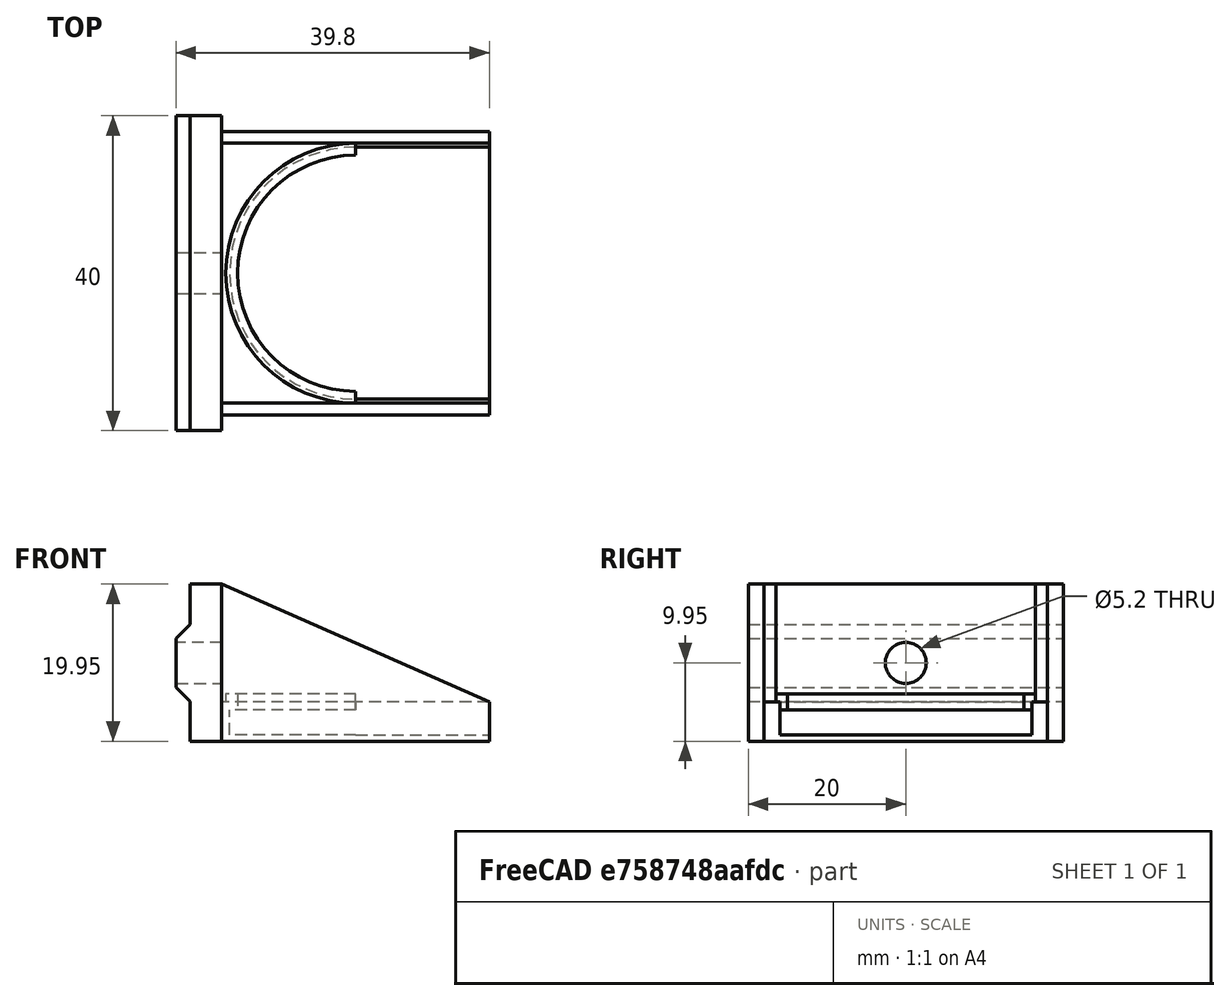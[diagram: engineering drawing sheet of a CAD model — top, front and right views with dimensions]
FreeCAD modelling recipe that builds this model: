
FCSTD DOCUMENT  (FreeCAD 1.0R39109 (Git))
Label: plotter_magnet_mount
License: All rights reserved
LicenseURL: https://en.wikipedia.org/wiki/All_rights_reserved
objects: Sketcher::SketchObject×7, PartDesign::Pad×5, PartDesign::Pocket×2, Mesh::Feature×1, PartDesign::LinearPattern×1, PartDesign::Body×1
note: 38 computed .brp shape members not serialized (recipe doc carries the construction recipe); baked Part::Feature solids carry a one-line shape summary decoded from their .brp

FEATURE [Mesh::Feature] _0x20_v_slot  label="20x20_v-slot"
FEATURE [Sketcher::SketchObject] Sketch
  ArcFitTolerance = 1e-06
  AttachmentSupport = -> [XZ_Plane]
  FullyConstrained = false
  MakeInternals = false
  MapMode = 5
  Placement = pos=(0,0,0) rot=(1,0,0;1.5708rad)
  sketch-geometry (5):
    g0: GeomPoint X=-20 Y=10 Z=0
    g1: LineSegment StartX=10.1727 StartY=4.9 StartZ=0 EndX=10.1727 EndY=-4.9 EndZ=0
    g2: LineSegment StartX=10.1727 StartY=-4.9 StartZ=0 EndX=8.37272 EndY=-3.1 EndZ=0
    g3: LineSegment StartX=8.37272 StartY=-3.1 StartZ=0 EndX=8.37272 EndY=3.1 EndZ=0
    g4: LineSegment StartX=8.37272 StartY=3.1 StartZ=0 EndX=10.1727 EndY=4.9 EndZ=0
  constraints (10):
    c: Coincident(g1,g2)
    c: Coincident(g2,g3)
    c: Coincident(g3,g4)
    c: Coincident(g4,g1)
    c: Equal(g2,g4)
    c: Parallel(g1,g3)
    c: DistanceY(g3,g3) = 6.2
    c: Perpendicular(g4,g2)
    c: Symmetric(g1,g1,g-1)
    c: DistanceX(g3,g1) = 1.8
FEATURE [PartDesign::Pad] Pad
  Direction = (0,-1,2e-16)
  Length = 40
  Length2 = 10
  Placement = pos=(0,0,0) rot=(1,0,0;1.5708rad)
  Profile = -> Sketch
  ReferenceAxis = -> Sketch [N_Axis]
  Refine = true
  Reversed = true
  Suppressed = false
  Type = 0
FEATURE [Sketcher::SketchObject] Sketch001
  ArcFitTolerance = 1e-06
  AttachmentSupport = -> [Pad]
  ExternalGeometry = -> [Pad]
  FullyConstrained = true
  MakeInternals = false
  MapMode = 5
  Placement = pos=(10.1727,0,0) rot=(0.707107,0,0.707107;3.14159rad)
  sketch-geometry (4):
    g0: LineSegment StartX=10 StartY=0 StartZ=0 EndX=-9.95 EndY=0 EndZ=0
    g1: LineSegment StartX=-9.95 StartY=0 StartZ=0 EndX=-9.95 EndY=-40 EndZ=0
    g2: LineSegment StartX=-9.95 StartY=-40 StartZ=0 EndX=10 EndY=-40 EndZ=0
    g3: LineSegment StartX=10 StartY=-40 StartZ=0 EndX=10 EndY=0 EndZ=0
  constraints (12):
    c: Coincident(g0,g1)
    c: Coincident(g1,g2)
    c: Coincident(g2,g3)
    c: Coincident(g3,g0)
    c: Horizontal(g0)
    c: Horizontal(g2)
    c: Vertical(g1)
    c: Vertical(g3)
    c: Distance(g1,g3) = 19.95
    c: PointOnObject(g0,g-1)
    c: DistanceX(g-1,g0) = 10
    c: DistanceY(g2,g-3) = 0
FEATURE [PartDesign::Pad] Pad001
  BaseFeature = -> Pad
  Direction = (1,0,-2e-16)
  Length = 4
  Length2 = 10
  Placement = pos=(0,0,0) rot=(1,0,0;1.5708rad)
  Profile = -> Sketch001
  ReferenceAxis = -> Sketch001 [N_Axis]
  Refine = true
  Suppressed = false
  Type = 0
FEATURE [Sketcher::SketchObject] Sketch002
  ArcFitTolerance = 1e-06
  AttachmentSupport = -> [Pad001]
  ExternalGeometry = -> [Pad001]
  FullyConstrained = true
  MakeInternals = false
  MapMode = 5
  Placement = pos=(14.1727,0,0) rot=(0.707107,0,0.707107;3.14159rad)
  sketch-geometry (5):
    g0: LineSegment StartX=-4.95 StartY=-2 StartZ=0 EndX=-9.95 EndY=-2 EndZ=0
    g1: LineSegment StartX=-9.95 StartY=-2 StartZ=0 EndX=-9.95 EndY=-38 EndZ=0
    g2: LineSegment StartX=-9.95 StartY=-38 StartZ=0 EndX=-4.95 EndY=-38 EndZ=0
    g3: LineSegment StartX=-4.95 StartY=-38 StartZ=0 EndX=-4.95 EndY=-2 EndZ=0
    g4: GeomPoint X=-9.95 Y=-20 Z=0
  constraints (13):
    c: Coincident(g0,g1)
    c: Coincident(g1,g2)
    c: Coincident(g2,g3)
    c: Coincident(g3,g0)
    c: Horizontal(g0)
    c: Horizontal(g2)
    c: Vertical(g1)
    c: Vertical(g3)
    c: DistanceY(g3,g3) = 36
    c: DistanceX(g0,g0) = 5
    c: Symmetric(g1,g1,g4)
    c: DistanceX(g-3,g1) = 0
    c: DistanceY(g-3,g1) = 2
FEATURE [PartDesign::Pad] Pad002
  BaseFeature = -> Pad001
  Direction = (1,0,-2e-16)
  Length = 34
  Length2 = 10
  Placement = pos=(0,0,0) rot=(1,0,0;1.5708rad)
  Profile = -> Sketch002
  ReferenceAxis = -> Sketch002 [N_Axis]
  Refine = true
  Suppressed = false
  Type = 0
FEATURE [Sketcher::SketchObject] Sketch003
  ArcFitTolerance = 1e-06
  AttachmentSupport = -> [Pad002]
  ExternalGeometry = -> [Pad002]
  FullyConstrained = true
  MakeInternals = false
  MapMode = 5
  Placement = pos=(-1.1e-15,-1.1e-15,-4.95) rot=(0,0,1;3.14159rad)
  sketch-geometry (4):
    g0: ArcOfCircle CenterX=-31.1727 CenterY=-20 CenterZ=0 NormalX=0 NormalY=0 NormalZ=1 AngleXU=0 Radius=16 StartAngle=4.71239 EndAngle=7.85398
    g1: ArcOfCircle CenterX=-71.1727 CenterY=-20 CenterZ=0 NormalX=0 NormalY=0 NormalZ=1 AngleXU=0 Radius=16 StartAngle=1.5708 EndAngle=4.71239
    g2: LineSegment StartX=-31.1727 StartY=-36 StartZ=0 EndX=-71.1727 EndY=-36 EndZ=0
    g3: LineSegment StartX=-31.1727 StartY=-4 StartZ=0 EndX=-71.1727 EndY=-4 EndZ=0
  constraints (9):
    c: Tangent(g0,g2) = 1.5708
    c: Tangent(g0,g3) = -1.5708
    c: Tangent(g1,g2) = 1.5708
    c: Tangent(g1,g3) = -1.5708
    c: Equal(g0,g1)
    c: Horizontal(g3)
    c: Distance(g0,g1) = 40
    c: Radius(g0) = 16
    c: Symmetric(g-3,g-4,g0)
FEATURE [PartDesign::Pocket] Pocket
  BaseFeature = -> Pad002
  Direction = (0,0,-1)
  Length = 4.2
  Length2 = 5
  Placement = pos=(0,0,0) rot=(1,0,0;1.5708rad)
  Profile = -> Sketch003
  ReferenceAxis = -> Sketch003 [N_Axis]
  Refine = true
  Suppressed = false
  Type = 0
FEATURE [Sketcher::SketchObject] Sketch004
  ArcFitTolerance = 1e-06
  AttachmentSupport = -> [Pocket]
  ExternalGeometry = -> [Pocket]
  FullyConstrained = true
  MakeInternals = false
  MapMode = 5
  Placement = pos=(14.1727,0,0) rot=(0.707107,0,0.707107;3.14159rad)
  sketch-geometry (3):
    g0: Circle CenterX=0 CenterY=-20 CenterZ=0 NormalX=0 NormalY=0 NormalZ=1 AngleXU=0 Radius=2.6
    g1: GeomPoint [constr] X=0.025 Y=-40 Z=0
    g2: GeomPoint [constr] X=0 Y=0 Z=0
  constraints (5):
    c: Diameter(g0) = 5.2
    c: Symmetric(g-3,g-3,g1)
    c: Coincident(g2,g-1)
    c: PointOnObject(g0,g-2)
    c: DistanceY(g0,g2) = 20
FEATURE [PartDesign::Pocket] Pocket001
  BaseFeature = -> Pocket
  Direction = (-1,0,2e-16)
  Length = 10
  Length2 = 5
  Placement = pos=(0,0,0) rot=(1,0,0;1.5708rad)
  Profile = -> Sketch004
  ReferenceAxis = -> Sketch004 [N_Axis]
  Refine = true
  Suppressed = false
  Type = 0
FEATURE [Sketcher::SketchObject] Sketch005
  ArcFitTolerance = 1e-06
  AttachmentSupport = -> [Pocket001]
  ExternalGeometry = -> [Pocket001]
  FullyConstrained = true
  MakeInternals = false
  MapMode = 5
  Placement = pos=(0,2,-4e-16) rot=(1,0,0;1.5708rad)
  sketch-geometry (3):
    g0: LineSegment StartX=14.1727 StartY=-4.95 StartZ=0 EndX=14.1727 EndY=10 EndZ=0
    g1: LineSegment StartX=14.1727 StartY=10 StartZ=0 EndX=48.1727 EndY=-4.95 EndZ=0
    g2: LineSegment StartX=48.1727 StartY=-4.95 StartZ=0 EndX=14.1727 EndY=-4.95 EndZ=0
  constraints (6):
    c: Coincident(g-3,g0)
    c: Coincident(g0,g-4)
    c: Coincident(g0,g1)
    c: Coincident(g1,g-3)
    c: Coincident(g1,g2)
    c: Coincident(g2,g0)
FEATURE [PartDesign::Pad] Pad003
  BaseFeature = -> Pocket001
  Direction = (0,-1,2e-16)
  Length = 1.5
  Length2 = 10
  Placement = pos=(0,0,0) rot=(1,0,0;1.5708rad)
  Profile = -> Sketch005
  ReferenceAxis = -> Sketch005 [N_Axis]
  Refine = true
  Reversed = true
  Suppressed = false
  Type = 0
FEATURE [PartDesign::LinearPattern] LinearPattern
  BaseFeature = -> Pad003
  Direction = -> Y_Axis
  Length = 34.5
  Mode = 0
  Occurrences = 2
  Offset = 34.5
  Originals = -> [Pad003]
  Placement = pos=(0,0,0) rot=(1,0,0;1.5708rad)
  Refine = true
  Suppressed = false
  TransformMode = 0
FEATURE [Sketcher::SketchObject] Sketch006
  ArcFitTolerance = 1e-06
  AttachmentSupport = -> [LinearPattern]
  ExternalGeometry = -> [LinearPattern]
  FullyConstrained = true
  MakeInternals = false
  MapMode = 5
  Placement = pos=(-1.1e-15,-1.1e-15,-4.95) rot=(0,0,1;3.14159rad)
  sketch-geometry (6):
    g0: ArcOfCircle CenterX=-31.1727 CenterY=-20 CenterZ=0 NormalX=0 NormalY=0 NormalZ=1 AngleXU=0 Radius=15 StartAngle=4.71239 EndAngle=7.85398
    g1: GeomPoint [constr] X=-31.1727 Y=-3.5 Z=0
    g2: GeomPoint [constr] X=-31.1727 Y=-36.5 Z=0
    g3: ArcOfCircle CenterX=-31.1727 CenterY=-20 CenterZ=0 NormalX=0 NormalY=0 NormalZ=1 AngleXU=0 Radius=16.5 StartAngle=4.71239 EndAngle=7.85398
    g4: LineSegment StartX=-31.1727 StartY=-5 StartZ=0 EndX=-31.1727 EndY=-3.5 EndZ=0
    g5: LineSegment StartX=-31.1727 StartY=-35 StartZ=0 EndX=-31.1727 EndY=-36.5 EndZ=0
  constraints (13):
    c: Radius(g0) = 15
    c: Symmetric(g-5,g-5,g1)
    c: Symmetric(g-4,g-4,g2)
    c: Angle(g3) = 3.14159
    c: Coincident(g3,g0)
    c: Coincident(g3,g1)
    c: Coincident(g3,g2)
    c: Coincident(g4,g0)
    c: Coincident(g4,g1)
    c: Vertical(g4)
    c: Coincident(g5,g0)
    c: Coincident(g5,g2)
    c: Vertical(g5)
FEATURE [PartDesign::Pad] Pad004
  BaseFeature = -> LinearPattern
  Direction = (0,0,1)
  Length = 2
  Length2 = 10
  Midplane = true
  Placement = pos=(0,0,0) rot=(1,0,0;1.5708rad)
  Profile = -> Sketch006
  ReferenceAxis = -> Sketch006 [N_Axis]
  Refine = true
  Suppressed = false
  Type = 0
FEATURE [PartDesign::Body] Body  label="plotter_magnet_mount"
  AllowCompound = false
  Group = -> [Sketch,Pad,Sketch001,Pad001,Sketch002,Pad002,Sketch003,Pocket,Sketch004,Pocket001,Sketch005,Pad003,LinearPattern,Sketch006,Pad004]
  Origin = -> Origin
  Tip = -> Pad004
